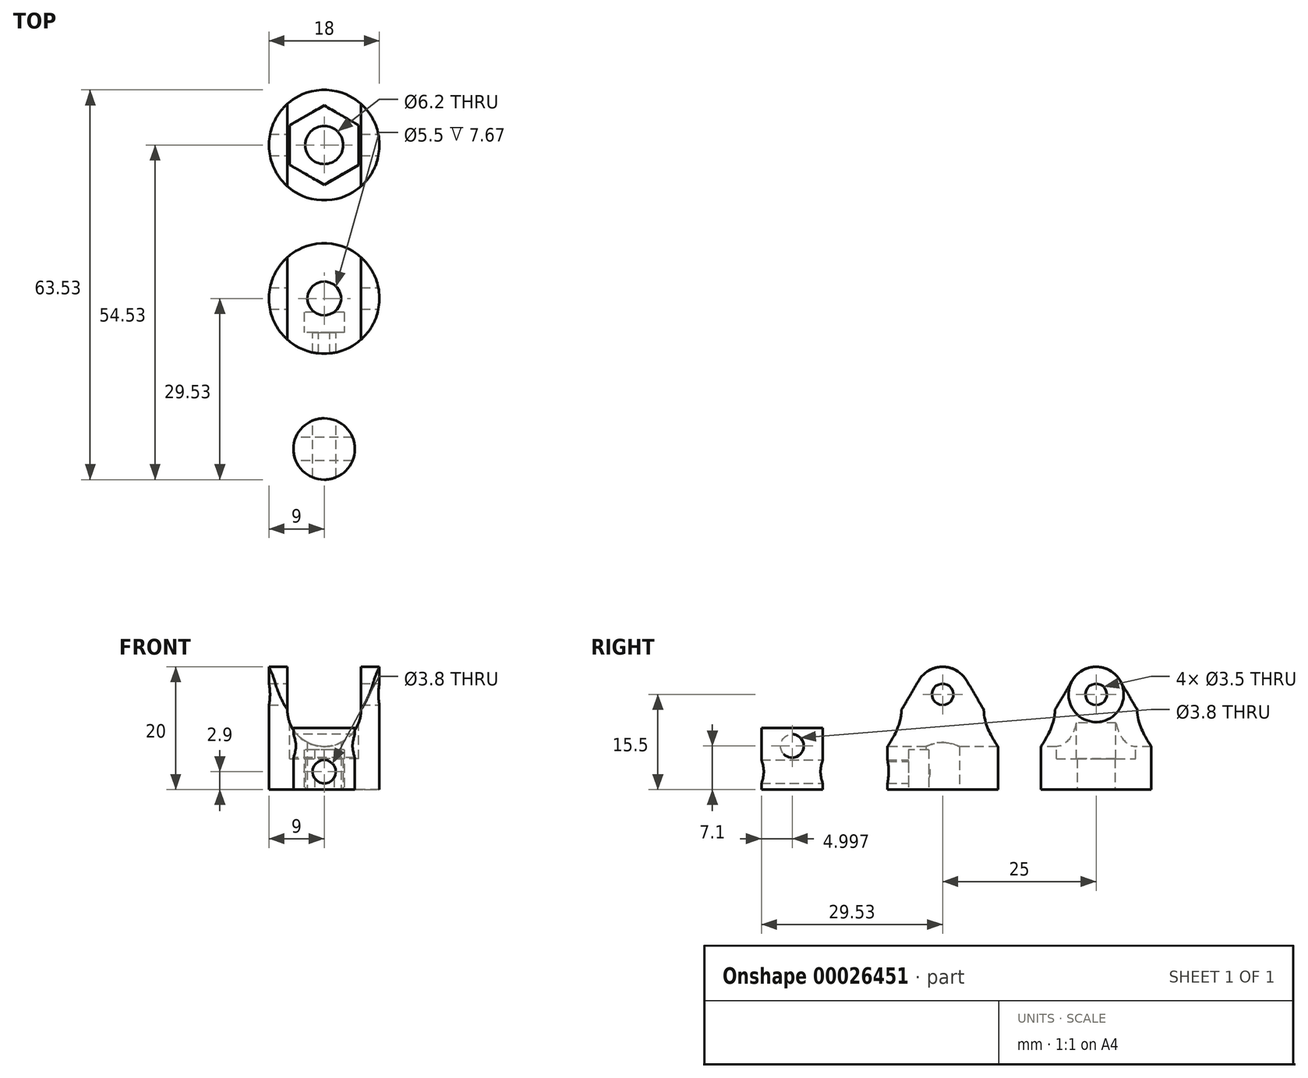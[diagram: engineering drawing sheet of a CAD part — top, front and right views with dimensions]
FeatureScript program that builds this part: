
annotation { "Feature Type Name" : "Feature", "Feature Type Description" : "" }
export const myFeature = defineFeature(function(context is Context, id is Id, definition is map)
    precondition{}
    {
        {
            var Q0;
            Q0=qCreatedBy(makeId("Top.planeOp"),FACE);
            var sketch = newSketch(context, id + "F0", { "sketchPlane" : qUnion([Q0])});
            skCircle(sketch, "E0", {"center": v(0, 0) * mm, "radius": 9 * mm});
            skSolve(sketch);
        }
        {
            var Q0;
            Q0=makeQuery(id+"F0.imprint","IMPRINT",FACE,{"disambiguationData":[TD([[makeQuery(id+"F0.imprint","IMPRINT",EDGE,{"derivedFrom":sQuery(id+"F0.wireOp",EDGE,"E0")}),1.0]])]});
            extrude(context, id + "F1", {"entities" : qUnion([Q0]), "depth" : 20 * mm});
        }
        {
            var Q0;
            Q0=qCreatedBy(makeId("Front.planeOp"),FACE);
            var sketch = newSketch(context, id + "F2", { "sketchPlane" : qUnion([Q0])});
            skCircle(sketch, "E1", {"center": v(0, 13) * mm, "radius": 6 * mm});
            skLineSegment(sketch, "E2.bottom", {"start": v(-6, 13) * mm, "end": v(6, 13) * mm});
            skLineSegment(sketch, "E2.top", {"start": v(-6, 21) * mm, "end": v(6, 21) * mm});
            skLineSegment(sketch, "E2.left", {"start": v(-6, 13) * mm, "end": v(-6, 21) * mm});
            skLineSegment(sketch, "E2.right", {"start": v(6, 13) * mm, "end": v(6, 21) * mm});
            skLineSegment(sketch, "E3.0", {"start": v(-9, 20) * mm, "end": v(9, 20) * mm, "construction": true});
            skLineSegment(sketch, "E3.1", {"start": v(-9, 0) * mm, "end": v(9, 0) * mm, "construction": true});
            skSolve(sketch);
        }
        {
            var Q0;
            Q0 = qSketchRegion(id + "F2", true);
            extrude(context, id + "F3", {"entities" : qUnion([Q0]), "operationType" : NewBodyOperationType.REMOVE, "endBound" : BoundingType.THROUGH_ALL, "oppositeDirection" : true, "depth" : 25 * mm, "hasSecondDirection" : true, "secondDirectionBound" : BoundingType.THROUGH_ALL, "secondDirectionOppositeDirection" : false, "secondDirectionDepth" : 25 * mm});
        }
        {
            var Q0;
            Q0=qCreatedBy(makeId("Right.planeOp"),FACE);
            var sketch = newSketch(context, id + "F4", { "sketchPlane" : qUnion([Q0])});
            skCircle(sketch, "E4", {"center": v(0, 15.5) * mm, "radius": 4.5 * mm});
            skLineSegment(sketch, "E5.0", {"start": v(-6.7, 20) * mm, "end": v(-6.7, 13) * mm});
            skCircle(sketch, "E6", {"center": v(0, 15.5) * mm, "radius": 1.75 * mm});
            skLineSegment(sketch, "E7", {"start": v(3.87, 17.8) * mm, "end": v(6.7, 13) * mm});
            skLineSegment(sketch, "E8", {"start": v(-3.87, 17.8) * mm, "end": v(-6.7, 13) * mm});
            skLineSegment(sketch, "E9.1", {"start": v(-6.7, 20) * mm, "end": v(6.7, 20) * mm});
            skLineSegment(sketch, "E10.0", {"start": v(6.7, 13) * mm, "end": v(6.7, 20) * mm});
            skSolve(sketch);
        }
        {
            var Q0;
            Q0=makeQuery(id+"F4.imprint","IMPRINT",FACE,{"disambiguationData":[TD([[makeQuery(id+"F4.imprint","IMPRINT",EDGE,{"derivedFrom":sQuery(id+"F4.wireOp",EDGE,"E6")}),1.0]])]});
            var Q1;
            {var subQ0=sQuery(id+"F4.wireOp",EDGE,"E8");Q1=makeQuery(id+"F4.imprint","IMPRINT",FACE,{"disambiguationData":[TD([[makeQuery(id+"F4.imprint","IMPRINT",EDGE,{"derivedFrom":subQ0}),-1.0]])]});}
            var Q2;
            {var subQ0=sQuery(id+"F4.wireOp",EDGE,"E7");Q2=makeQuery(id+"F4.imprint","IMPRINT",FACE,{"disambiguationData":[TD([[makeQuery(id+"F4.imprint","IMPRINT",EDGE,{"derivedFrom":subQ0}),1.0]])]});}
            extrude(context, id + "F5", {"entities" : qUnion([Q0, Q1, Q2]), "operationType" : NewBodyOperationType.REMOVE, "endBound" : BoundingType.THROUGH_ALL, "oppositeDirection" : true, "depth" : 25 * mm, "hasSecondDirection" : true, "secondDirectionBound" : BoundingType.THROUGH_ALL, "secondDirectionOppositeDirection" : false, "secondDirectionDepth" : 25 * mm});
        }
        {
            var Q0;
            Q0=makeQuery(id+"F1.opExtrude","SWEPT_BODY",BODY,{"disambiguationData":[OSD([sQuery(id+"F0.wireOp",EDGE,"E0")])]});
            transform(context, id + "F6", {"entities" : qUnion([Q0]), "transformType" : TransformType.TRANSLATION_3D, "dx" : 0 * mm, "dy" : 25 * mm, "dz" : 0 * mm, "makeCopy" : true});
        }
        {
            var Q0;
            Q0=makeQuery(id+"F1.opExtrude","CAP_FACE",FACE,{"disambiguationData":[OSD([sQuery(id+"F0.wireOp",EDGE,"E0")])],"isStart":true});
            var sketch = newSketch(context, id + "F7", { "sketchPlane" : qUnion([Q0])});
            skCircle(sketch, "E11", {"center": v(0, 0) * mm, "radius": 2.75 * mm});
            skLineSegment(sketch, "E12.rect.bottom", {"start": v(3.25, 2.25) * mm, "end": v(-3.25, 2.25) * mm});
            skLineSegment(sketch, "E12.rect.top", {"start": v(3.25, 5.55) * mm, "end": v(-3.25, 5.55) * mm});
            skLineSegment(sketch, "E12.rect.left", {"start": v(3.25, 2.25) * mm, "end": v(3.25, 5.55) * mm});
            skLineSegment(sketch, "E12.rect.right", {"start": v(-3.25, 2.25) * mm, "end": v(-3.25, 5.55) * mm});
            skPoint(sketch, "E12.rect.middle", {"position": v(0, 3.9) * mm});
            skSolve(sketch);
        }
        {
            var Q0;
            {var subQ0=sQuery(id+"F7.wireOp",EDGE,"E12.rect.bottom");var subQ1=sQuery(id+"F7.wireOp",EDGE,"E11");var subQ2=makeQuery(id+"F7.imprint","INTERSECT",VERTEX,{"disambiguationData":[OD(0.0)],"derivedFrom":[subQ1,subQ0]});Q0=makeQuery(id+"F7.imprint","IMPRINT",FACE,{"disambiguationData":[TD([[makeQuery(id+"F7.imprint","IMPRINT",EDGE,{"disambiguationData":[TD([[subQ2,1.0]])],"derivedFrom":subQ1}),1.0]])]});}
            var Q1;
            {var subQ0=sQuery(id+"F7.wireOp",EDGE,"E12.rect.bottom");var subQ1=sQuery(id+"F7.wireOp",EDGE,"E11");var subQ2=makeQuery(id+"F7.imprint","INTERSECT",VERTEX,{"disambiguationData":[OD(0.0)],"derivedFrom":[subQ1,subQ0]});Q1=makeQuery(id+"F7.imprint","IMPRINT",FACE,{"disambiguationData":[TD([[makeQuery(id+"F7.imprint","IMPRINT",EDGE,{"disambiguationData":[TD([[subQ2,-1.0]])],"derivedFrom":subQ1}),1.0]])]});}
            extrude(context, id + "F8", {"entities" : qUnion([Q0, Q1]), "operationType" : NewBodyOperationType.REMOVE, "endBound" : BoundingType.THROUGH_ALL, "oppositeDirection" : true, "depth" : 25 * mm});
        }
        {
            var Q0;
            Q0=makeQuery(id+"F7.imprint","IMPRINT",FACE,{"disambiguationData":[TD([[makeQuery(id+"F7.imprint","IMPRINT",EDGE,{"derivedFrom":sQuery(id+"F7.wireOp",EDGE,"E12.rect.top")}),1.0]])]});
            extrude(context, id + "F9", {"entities" : qUnion([Q0]), "operationType" : NewBodyOperationType.REMOVE, "oppositeDirection" : true, "depth" : 6.5 * mm});
        }
        {
            var Q0;
            Q0=makeQuery(id+"F9.boolean.opBoolean","COPY",FACE,{"derivedFrom":makeQuery(id+"F9.opExtrude","SWEPT_FACE",FACE,{"disambiguationData":[OSD([sQuery(id+"F7.wireOp",EDGE,"E12.rect.top")])]})});
            var sketch = newSketch(context, id + "F10", { "sketchPlane" : qUnion([Q0])});
            skCircle(sketch, "E13", {"center": v(0, 3.25) * mm, "radius": 1.6 * mm});
            skPoint(sketch, "E14", {"position": v(3.25, 3.25) * mm});
            skSolve(sketch);
        }
        {
            var Q0;
            Q0=makeQuery(id+"F10.imprint","IMPRINT",FACE,{"disambiguationData":[TD([[makeQuery(id+"F10.imprint","IMPRINT",EDGE,{"derivedFrom":sQuery(id+"F10.wireOp",EDGE,"E13")}),1.0]])]});
            extrude(context, id + "F11", {"entities" : qUnion([Q0]), "operationType" : NewBodyOperationType.REMOVE, "endBound" : BoundingType.THROUGH_ALL, "oppositeDirection" : true, "depth" : 25 * mm});
        }
        {
            var Q0;
            Q0=makeQuery(id+"F6.opPattern","COPY",FACE,{"derivedFrom":makeQuery(id+"F1.opExtrude","CAP_FACE",FACE,{"disambiguationData":[OSD([sQuery(id+"F0.wireOp",EDGE,"E0")])],"isStart":true}),"instanceName":"1"});
            var sketch = newSketch(context, id + "F12", { "sketchPlane" : qUnion([Q0])});
            skCircle(sketch, "E15", {"center": v(0, -25) * mm, "radius": 3.1 * mm});
            skSolve(sketch);
        }
        {
            var Q0;
            Q0=makeQuery(id+"F12.imprint","IMPRINT",FACE,{"disambiguationData":[TD([[makeQuery(id+"F12.imprint","IMPRINT",EDGE,{"derivedFrom":sQuery(id+"F12.wireOp",EDGE,"E15")}),1.0]])]});
            extrude(context, id + "F13", {"entities" : qUnion([Q0]), "operationType" : NewBodyOperationType.REMOVE, "endBound" : BoundingType.THROUGH_ALL, "oppositeDirection" : true, "depth" : 25 * mm});
        }
        {
            var Q0;
            Q0=sQuery(id+"F2.wireOp",EDGE,"E2.bottom");
            var Q1;
            Q1=sQuery(id+"F2.wireOp",EDGE,"E1");
            cPlane(context, id + "F14", {"entities" : qUnion([Q0, Q1]), "cplaneType" : CPlaneType.LINE_ANGLE, "offset" : 150 * mm, "angle" : 0 * degree, "width" : 150 * mm, "height" : 150 * mm});
        }
        {
            var Q0;
            Q0=qCreatedBy(id+"F14.planeOp",FACE);
            var sketch = newSketch(context, id + "F15", { "sketchPlane" : qUnion([Q0])});
            skCircle(sketch, "E16.0", {"center": v(0, -25) * mm, "radius": 3.1 * mm, "construction": true});
            skCircle(sketch, "E17.cCircle", {"center": v(0, -25) * mm, "radius": 5.6 * mm, "construction": true});
            skLineSegment(sketch, "E17.0", {"start": v(5.6, -28.23) * mm, "end": v(0, -31.47) * mm});
            skLineSegment(sketch, "E17.1", {"start": v(0, -31.47) * mm, "end": v(-5.6, -28.23) * mm});
            skLineSegment(sketch, "E17.2", {"start": v(-5.6, -28.23) * mm, "end": v(-5.6, -21.77) * mm});
            skLineSegment(sketch, "E17.3", {"start": v(-5.6, -21.77) * mm, "end": v(0, -18.53) * mm});
            skLineSegment(sketch, "E17.4", {"start": v(0, -18.53) * mm, "end": v(5.6, -21.77) * mm});
            skLineSegment(sketch, "E17.5", {"start": v(5.6, -21.77) * mm, "end": v(5.6, -28.23) * mm});
            skPoint(sketch, "E17.0.midPoint", {"position": v(2.8, -29.85) * mm});
            skSolve(sketch);
        }
        {
            var Q0;
            Q0 = qSketchRegion(id + "F15", true);
            extrude(context, id + "F16", {"entities" : qUnion([Q0]), "operationType" : NewBodyOperationType.REMOVE, "depth" : 8 * mm});
        }
        {
            var Q0;
            Q0=qCreatedBy(makeId("Top.planeOp"),FACE);
            var sketch = newSketch(context, id + "F17", { "sketchPlane" : qUnion([Q0])});
            skCircle(sketch, "E18", {"center": v(0, -24.53) * mm, "radius": 5 * mm});
            skSolve(sketch);
        }
        {
            var Q0;
            Q0=makeQuery(id+"F17.imprint","IMPRINT",FACE,{"disambiguationData":[TD([[makeQuery(id+"F17.imprint","IMPRINT",EDGE,{"derivedFrom":sQuery(id+"F17.wireOp",EDGE,"E18")}),1.0]])]});
            extrude(context, id + "F18", {"entities" : qUnion([Q0]), "depth" : 10 * mm});
        }
        {
            var Q0;
            Q0=qCreatedBy(makeId("Front.planeOp"),FACE);
            var sketch = newSketch(context, id + "F19", { "sketchPlane" : qUnion([Q0])});
            skCircle(sketch, "E19", {"center": v(0, 2.9) * mm, "radius": 1.9 * mm});
            skSolve(sketch);
        }
        {
            var Q0;
            Q0 = qSketchRegion(id + "F19", true);
            extrude(context, id + "F20", {"entities" : qUnion([Q0]), "operationType" : NewBodyOperationType.REMOVE, "endBound" : BoundingType.THROUGH_ALL, "depth" : 25 * mm});
        }
        {
            var Q0;
            Q0=qCreatedBy(makeId("Right.planeOp"),FACE);
            var sketch = newSketch(context, id + "F21", { "sketchPlane" : qUnion([Q0])});
            skCircle(sketch, "E20", {"center": v(-24.53, 7.1) * mm, "radius": 1.9 * mm});
            skPoint(sketch, "E20.centerSnap0", {"position": v(-24.53, 10) * mm});
            skLineSegment(sketch, "E21.0", {"start": v(-28.53, 10) * mm, "end": v(-20.53, 10) * mm});
            skSolve(sketch);
        }
        {
            var Q0;
            Q0 = qSketchRegion(id + "F21", true);
            var Q1;
            Q1=sQuery(id+"F21.wireOp",EDGE,"E20");
            extrude(context, id + "F22", {"entities" : qUnion([Q0]), "operationType" : NewBodyOperationType.REMOVE, "surfaceEntities" : qUnion([Q1]), "endBound" : BoundingType.THROUGH_ALL, "depth" : 25 * mm, "hasSecondDirection" : true, "secondDirectionBound" : BoundingType.THROUGH_ALL, "secondDirectionOppositeDirection" : true, "secondDirectionDepth" : 25 * mm});
        }
    });
